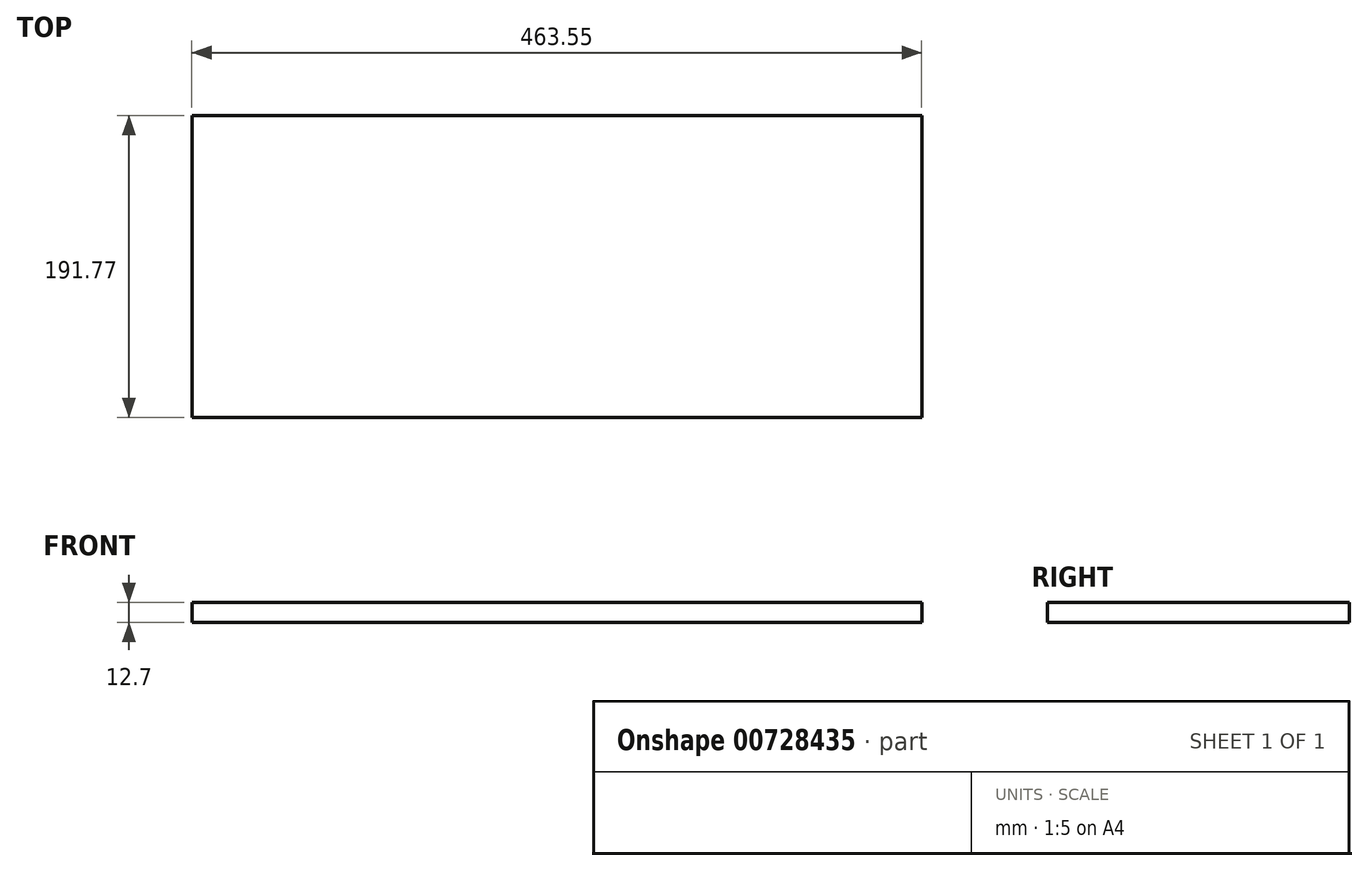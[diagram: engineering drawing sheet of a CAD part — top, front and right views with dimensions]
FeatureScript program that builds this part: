
annotation { "Feature Type Name" : "Feature", "Feature Type Description" : "" }
export const myFeature = defineFeature(function(context is Context, id is Id, definition is map)
    precondition{}
    {
        {
            var Q0;
            Q0=qCreatedBy(makeId("Top.planeOp"),FACE);
            var sketch = newSketch(context, id + "F0", { "sketchPlane" : qUnion([Q0])});
            skLineSegment(sketch, "E0.bottom", {"start": v(-171.56, 75.23) * mm, "end": v(292, 75.23) * mm});
            skLineSegment(sketch, "E0.top", {"start": v(-171.56, -116.54) * mm, "end": v(292, -116.54) * mm});
            skLineSegment(sketch, "E0.left", {"start": v(-171.56, 75.23) * mm, "end": v(-171.56, -116.54) * mm});
            skLineSegment(sketch, "E0.right", {"start": v(292, 75.23) * mm, "end": v(292, -116.54) * mm});
            skSolve(sketch);
        }
        {
            var Q0;
            Q0 = qSketchRegion(id + "F0", true);
            extrude(context, id + "F1", {"entities" : qUnion([Q0]), "depth" : 12.7 * mm, "offsetDistance" : 25.4 * mm});
        }
    });
